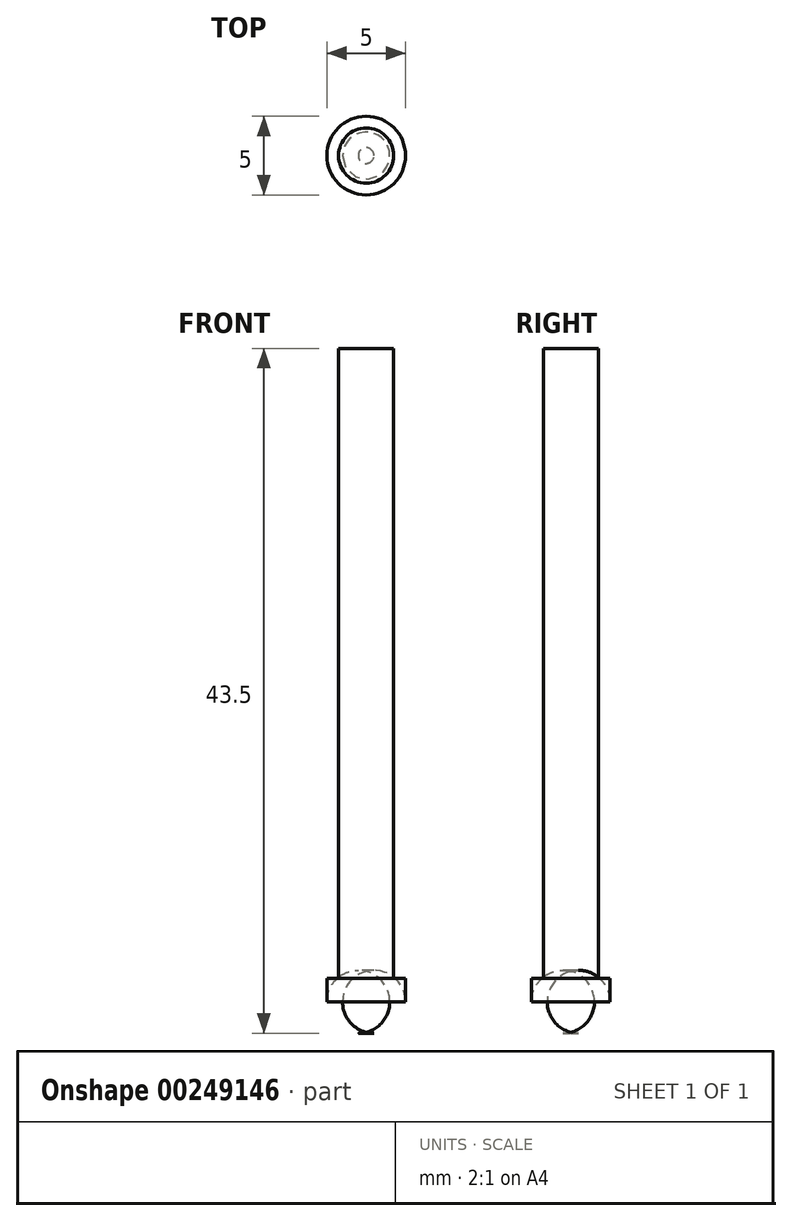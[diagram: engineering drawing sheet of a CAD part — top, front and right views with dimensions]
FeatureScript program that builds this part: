
annotation { "Feature Type Name" : "Feature", "Feature Type Description" : "" }
export const myFeature = defineFeature(function(context is Context, id is Id, definition is map)
    precondition{}
    {
        {
            var Q0;
            Q0=qCreatedBy(makeId("Top.planeOp"),FACE);
            var sketch = newSketch(context, id + "F0", { "sketchPlane" : qUnion([Q0])});
            skCircle(sketch, "E0", {"center": v(0, 0) * mm, "radius": 1.75 * mm});
            skCircle(sketch, "E1", {"center": v(0, 0) * mm, "radius": 2.5 * mm});
            skSolve(sketch);
        }
        {
            var Q0;
            Q0=makeQuery(id+"F0.imprint","IMPRINT",FACE,{"disambiguationData":[TD([[makeQuery(id+"F0.imprint","IMPRINT",EDGE,{"derivedFrom":sQuery(id+"F0.wireOp",EDGE,"E0")}),1.0]])]});
            var Q1;
            Q1=sQuery(id+"F0.wireOp",EDGE,"E0");
            extrude(context, id + "F1", {"entities" : qUnion([Q0]), "surfaceEntities" : qUnion([Q1]), "depth" : 40 * mm});
        }
        {
            var Q0;
            Q0=makeQuery(id+"F0.imprint","IMPRINT",FACE,{"disambiguationData":[TD([[makeQuery(id+"F0.imprint","IMPRINT",EDGE,{"derivedFrom":sQuery(id+"F0.wireOp",EDGE,"E0")}),1.0]])]});
            var Q1;
            Q1=makeQuery(id+"F0.imprint","IMPRINT",FACE,{"disambiguationData":[TD([[makeQuery(id+"F0.imprint","IMPRINT",EDGE,{"derivedFrom":sQuery(id+"F0.wireOp",EDGE,"E0")}),-1.0]])]});
            extrude(context, id + "F2", {"entities" : qUnion([Q0, Q1]), "operationType" : NewBodyOperationType.ADD, "oppositeDirection" : true, "depth" : 3.5 * mm});
        }
        {
            var Q0;
            Q0=makeQuery(id+"F2.opExtrude","CAP_EDGE",EDGE,{"disambiguationData":[OSD([sQuery(id+"F0.wireOp",EDGE,"E1")])],"isStart":false});
            fillet(context, id + "F3", {"entities" : qUnion([Q0]), "radius" : 2 * mm, "tangentPropagation" : true, "allowEdgeOverflow" : false});
        }
    });
